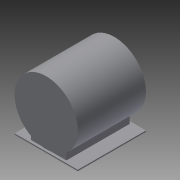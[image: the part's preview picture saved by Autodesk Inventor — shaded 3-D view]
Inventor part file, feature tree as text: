
AUTODESK INVENTOR PART (.ipt)
format: ipt  version: 2015 SP1 (Build 190203100, 203)  size: 163,328 bytes
history: native  units: in
note: dims shown in document units (in); Inventor stores cm internally (conversion verified against a paired STEP export)
features: sketch x7, extrude x5, plane x3, hole x1, projected_geometry x1
ambient origin geometry x8: Origin, YZ Plane, XZ Plane, XY Plane, X Axis, Y Axis, Z Axis, Center Point
bodies: Solid1 (feature_tree)
feature tree (17):
  extrude  "Extrusion1"  Depth=0.1in
  extrude  "Extrusion2"  Depth=2.0in
  hole  "Hole1"  [1 undecoded]
  plane  "Work Plane2"
  extrude  "Extrusion3"  TaperAngle=0.0deg  [1 undecoded]
  plane  "Work Plane7"
  extrude  "Extrusion4"  TaperAngle=45.0deg  [1 undecoded]
  plane  "Work Plane9"
  extrude  "Extrusion5"  TaperAngle=135.0deg  [1 undecoded]
  sketch  "Sketch7"  dims[d12=135.0deg d13=0.196in d14=0.5in d15=0.375in d16=0.25in d17=0.5635in d18=0.75in d19=0.8108in d20=6.5in d21=0.25in d22=3.65in d23=1.0in d24=0.0in d27=0.206in d28=0.0in d29=0.125in d30=0.0in d31=0.333in d32=0.5115in d33=0.9355in d38=0.333in d39=0.333in d40=0.902in d41=0.333in d46=0.266in d47=0.3665in d50=0.4975in d51=0.3365in d52=0.125in d53=0.0in]
  sketch  "Sketch1"  dims[d0=0.625in d1=0.1in]
  sketch  "Sketch2"  dims[d2=0.191in d3=2.0in]
  sketch  "Sketch3"  dims[d4=0.0in d5=6.5in]
  sketch  "Sketch4"  dims[d6=7.0in d7=0.0in]
  projected_geometry  "Projected Loop1"
  sketch  "Sketch5"  dims[d8=5.75in d9=45.0deg]
  sketch  "Sketch6"  dims[d10=45.0deg d11=135.0deg]
note: 4 required parameter values undecoded (feature->parameter linkage not recoverable at this tier; creation-order binding heuristic only, values carry confidence <= 0.55)
